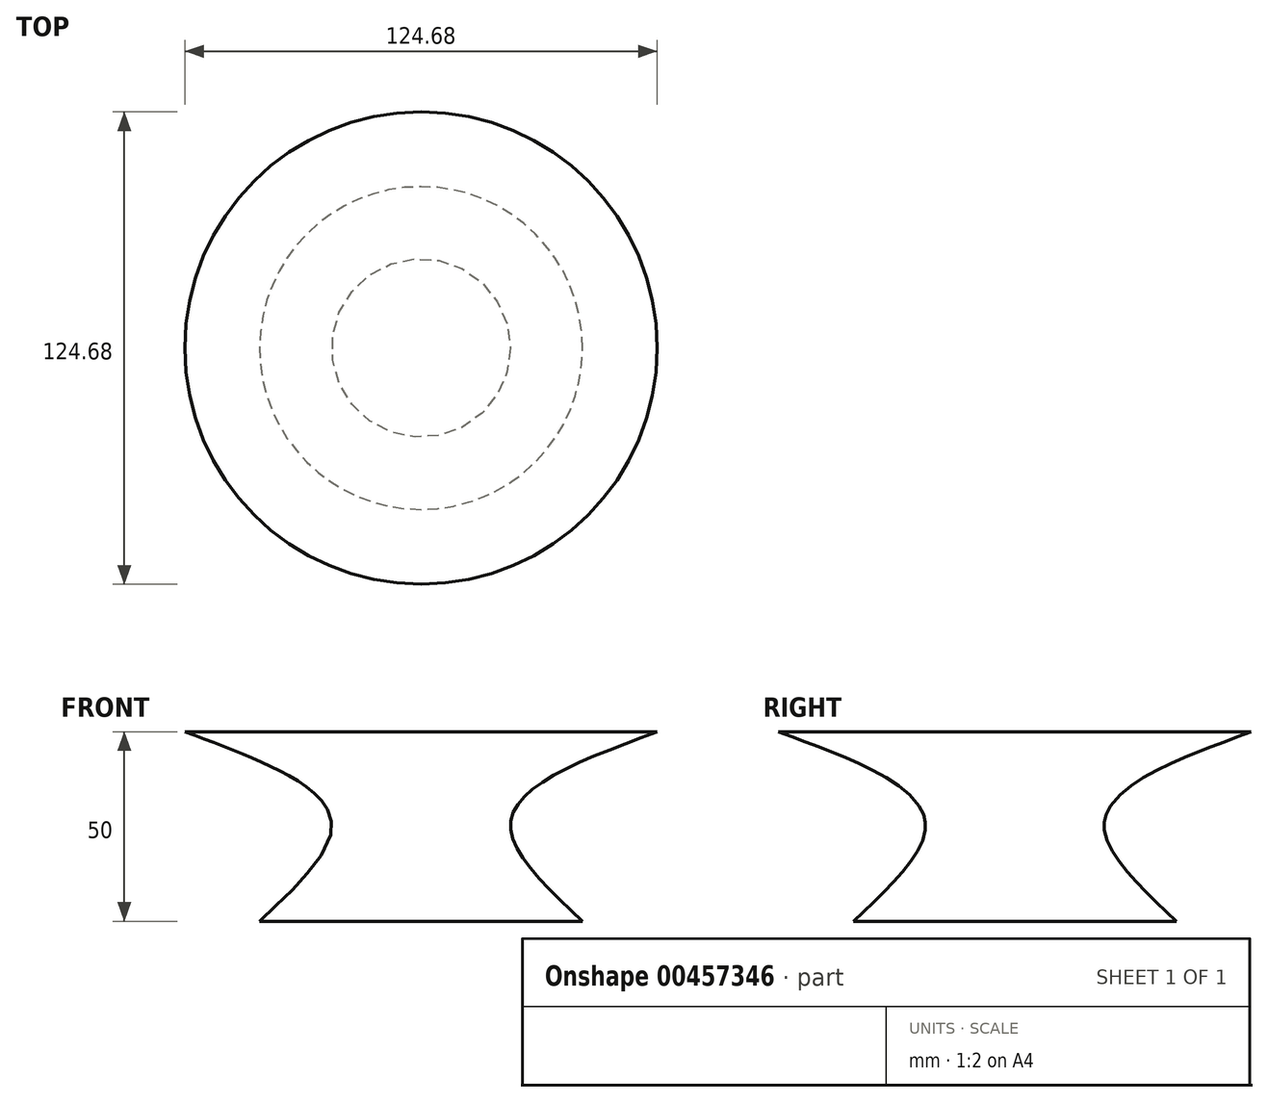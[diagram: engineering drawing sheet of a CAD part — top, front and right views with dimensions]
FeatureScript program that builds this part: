
annotation { "Feature Type Name" : "Feature", "Feature Type Description" : "" }
export const myFeature = defineFeature(function(context is Context, id is Id, definition is map)
    precondition{}
    {
        {
            var Q0;
            Q0=qCreatedBy(makeId("Top.planeOp"),FACE);
            cPlane(context, id + "F0", {"entities" : qUnion([Q0]), "cplaneType" : CPlaneType.OFFSET, "offset" : 25 * mm, "width" : 150 * mm, "height" : 150 * mm});
        }
        {
            var Q0;
            Q0=qCreatedBy(makeId("Top.planeOp"),FACE);
            cPlane(context, id + "F1", {"entities" : qUnion([Q0]), "cplaneType" : CPlaneType.OFFSET, "offset" : 50 * mm, "width" : 150 * mm, "height" : 150 * mm});
        }
        {
            var Q0;
            Q0=qCreatedBy(makeId("Top.planeOp"),FACE);
            var sketch = newSketch(context, id + "F2", { "sketchPlane" : qUnion([Q0])});
            skCircle(sketch, "E0", {"center": v(0, 0) * mm, "radius": 42.6 * mm});
            skSolve(sketch);
        }
        {
            var Q0;
            Q0=qCreatedBy(id+"F0.planeOp",FACE);
            var sketch = newSketch(context, id + "F3", { "sketchPlane" : qUnion([Q0])});
            skCircle(sketch, "E1", {"center": v(0, 0) * mm, "radius": 23.57 * mm});
            skSolve(sketch);
        }
        {
            var Q0;
            Q0=qCreatedBy(id+"F1.planeOp",FACE);
            var sketch = newSketch(context, id + "F4", { "sketchPlane" : qUnion([Q0])});
            skCircle(sketch, "E2", {"center": v(0, 0) * mm, "radius": 62.34 * mm});
            skSolve(sketch);
        }
        {
            var Q0;
            Q0=makeQuery(id+"F4.imprint","IMPRINT",FACE,{"disambiguationData":[TD([[makeQuery(id+"F4.imprint","IMPRINT",EDGE,{"derivedFrom":sQuery(id+"F4.wireOp",EDGE,"E2")}),1.0]])]});
            var Q1;
            Q1=makeQuery(id+"F3.imprint","IMPRINT",FACE,{"disambiguationData":[TD([[makeQuery(id+"F3.imprint","IMPRINT",EDGE,{"derivedFrom":sQuery(id+"F3.wireOp",EDGE,"E1")}),1.0]])]});
            var Q2;
            Q2=makeQuery(id+"F2.imprint","IMPRINT",FACE,{"disambiguationData":[TD([[makeQuery(id+"F2.imprint","IMPRINT",EDGE,{"derivedFrom":sQuery(id+"F2.wireOp",EDGE,"E0")}),1.0]])]});
            loft(context, id + "F5", {"sheetProfilesArray" : [{ "sheetProfileEntities" : qUnion([Q0]) }, { "sheetProfileEntities" : qUnion([Q1]) }, { "sheetProfileEntities" : qUnion([Q2]) }]});
        }
    });
